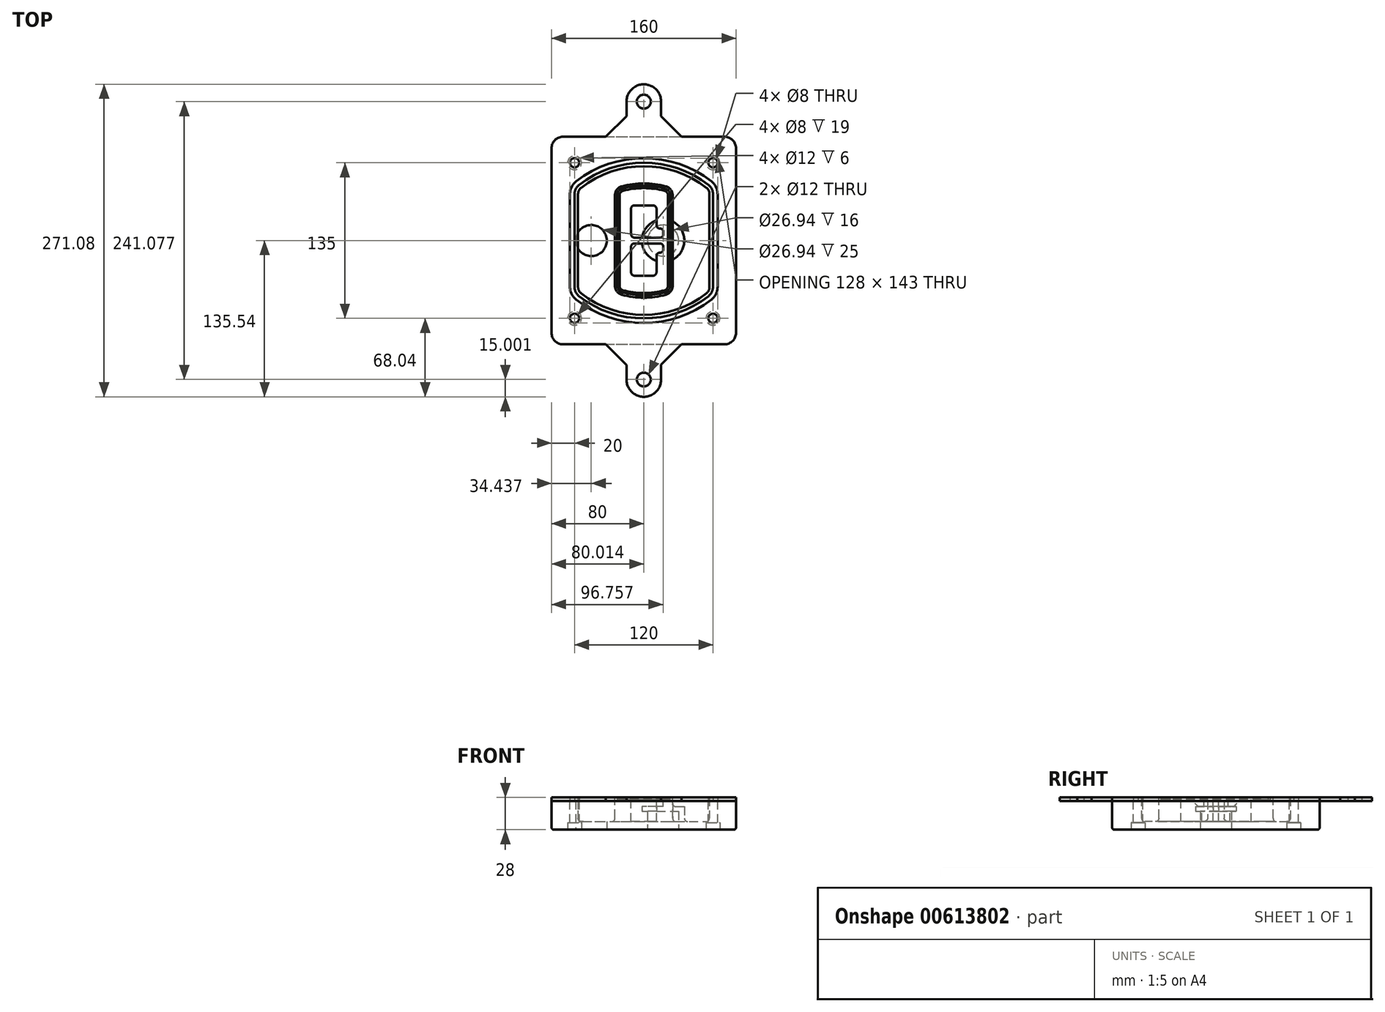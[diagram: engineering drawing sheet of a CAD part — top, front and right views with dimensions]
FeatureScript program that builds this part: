
annotation { "Feature Type Name" : "Feature", "Feature Type Description" : "" }
export const myFeature = defineFeature(function(context is Context, id is Id, definition is map)
    precondition{}
    {
        {
            var Q0;
            Q0=qCreatedBy(makeId("Top.planeOp"),FACE);
            var sketch = newSketch(context, id + "F0", { "sketchPlane" : qUnion([Q0])});
            skPoint(sketch, "E0.rect.middle", {"position": v(0, 0) * mm});
            skLineSegment(sketch, "E1.bottom", {"start": v(-70, -90) * mm, "end": v(70, -90) * mm});
            skLineSegment(sketch, "E1.top", {"start": v(-70, 90) * mm, "end": v(70, 90) * mm});
            skLineSegment(sketch, "E1.left", {"start": v(-80, -80) * mm, "end": v(-80, 80) * mm});
            skLineSegment(sketch, "E1.right", {"start": v(80, -80) * mm, "end": v(80, 80) * mm});
            skLineSegment(sketch, "E2", {"start": v(-80, 90) * mm, "end": v(80, -90) * mm, "construction": true});
            skLineSegment(sketch, "E3", {"start": v(80, 90) * mm, "end": v(-80, -90) * mm, "construction": true});
            skCircle(sketch, "E4", {"center": v(-60, 67.5) * mm, "radius": 4 * mm});
            skCircle(sketch, "E5", {"center": v(60, 67.5) * mm, "radius": 4 * mm});
            skCircle(sketch, "E6", {"center": v(60, -67.5) * mm, "radius": 4 * mm});
            skCircle(sketch, "E7", {"center": v(-60, -67.5) * mm, "radius": 4 * mm});
            skLineSegment(sketch, "E8", {"start": v(-60, 67.5) * mm, "end": v(60, 67.5) * mm, "construction": true});
            skLineSegment(sketch, "E9", {"start": v(60, 67.5) * mm, "end": v(60, -67.5) * mm, "construction": true});
            skLineSegment(sketch, "E10", {"start": v(60, -67.5) * mm, "end": v(-60, -67.5) * mm, "construction": true});
            skLineSegment(sketch, "E11", {"start": v(-60, -67.5) * mm, "end": v(-60, 67.5) * mm, "construction": true});
            skLineSegment(sketch, "E12", {"start": v(-60, 40.3) * mm, "end": v(-60, -40.3) * mm});
            skLineSegment(sketch, "E13", {"start": v(60, 40.3) * mm, "end": v(60, -40.3) * mm});
            skArc(sketch, "E14", {"start": v(56.15, 48.18) * mm, "mid": v(0, 67.5) * mm, "end": v(-56.15, 48.18) * mm});
            skArc(sketch, "E15", {"start": v(-56.15, -48.18) * mm, "mid": v(0, -67.5) * mm, "end": v(56.15, -48.18) * mm});
            skLineSegment(sketch, "E16", {"start": v(-60, 0) * mm, "end": v(60, 0) * mm, "construction": true});
            skPoint(sketch, "E17.visualSharp", {"position": v(-60, -45) * mm});
            skArc(sketch, "E17.filletArc", {"start": v(-60, -40.3) * mm, "mid": v(-58.99, -44.68) * mm, "end": v(-56.15, -48.18) * mm});
            skPoint(sketch, "E18.visualSharp", {"position": v(-60, 45) * mm});
            skArc(sketch, "E18.filletArc", {"start": v(-56.15, 48.18) * mm, "mid": v(-58.99, 44.68) * mm, "end": v(-60, 40.3) * mm});
            skPoint(sketch, "E19.visualSharp", {"position": v(60, 45) * mm});
            skArc(sketch, "E19.filletArc", {"start": v(60, 40.3) * mm, "mid": v(58.99, 44.68) * mm, "end": v(56.15, 48.18) * mm});
            skPoint(sketch, "E20.visualSharp", {"position": v(60, -45) * mm});
            skArc(sketch, "E20.filletArc", {"start": v(56.15, -48.18) * mm, "mid": v(58.99, -44.68) * mm, "end": v(60, -40.3) * mm});
            skPoint(sketch, "E21.visualSharp", {"position": v(-80, 90) * mm});
            skArc(sketch, "E21.filletArc", {"start": v(-70, 90) * mm, "mid": v(-77.07, 87.07) * mm, "end": v(-80, 80) * mm});
            skPoint(sketch, "E22.visualSharp", {"position": v(80, 90) * mm});
            skArc(sketch, "E22.filletArc", {"start": v(80, 80) * mm, "mid": v(77.07, 87.07) * mm, "end": v(70, 90) * mm});
            skPoint(sketch, "E23.visualSharp", {"position": v(80, -90) * mm});
            skArc(sketch, "E23.filletArc", {"start": v(70, -90) * mm, "mid": v(77.07, -87.07) * mm, "end": v(80, -80) * mm});
            skPoint(sketch, "E24.visualSharp", {"position": v(-80, -90) * mm});
            skArc(sketch, "E24.filletArc", {"start": v(-80, -80) * mm, "mid": v(-77.07, -87.07) * mm, "end": v(-70, -90) * mm});
            skArc(sketch, "E25.0", {"start": v(57, 40.3) * mm, "mid": v(56.3, 43.36) * mm, "end": v(54.3, 45.81) * mm});
            skLineSegment(sketch, "E25.1", {"start": v(57, 40.3) * mm, "end": v(57, -40.3) * mm});
            skArc(sketch, "E25.2", {"start": v(54.3, -45.81) * mm, "mid": v(56.3, -43.36) * mm, "end": v(57, -40.3) * mm});
            skArc(sketch, "E25.3", {"start": v(-54.3, -45.81) * mm, "mid": v(0, -64.5) * mm, "end": v(54.3, -45.81) * mm});
            skArc(sketch, "E25.4", {"start": v(-57, -40.3) * mm, "mid": v(-56.3, -43.36) * mm, "end": v(-54.3, -45.81) * mm});
            skArc(sketch, "E25.5", {"start": v(54.3, 45.81) * mm, "mid": v(0, 64.5) * mm, "end": v(-54.3, 45.81) * mm});
            skLineSegment(sketch, "E25.6", {"start": v(-57, 40.3) * mm, "end": v(-57, -40.3) * mm});
            skArc(sketch, "E25.7", {"start": v(-54.3, 45.81) * mm, "mid": v(-56.3, 43.36) * mm, "end": v(-57, 40.3) * mm});
            skArc(sketch, "E26.0", {"start": v(-58.62, 51.33) * mm, "mid": v(-62.58, 46.43) * mm, "end": v(-64, 40.3) * mm});
            skArc(sketch, "E26.1", {"start": v(58.62, 51.33) * mm, "mid": v(0, 71.5) * mm, "end": v(-58.62, 51.33) * mm});
            skArc(sketch, "E26.2", {"start": v(64, 40.3) * mm, "mid": v(62.58, 46.43) * mm, "end": v(58.62, 51.33) * mm});
            skLineSegment(sketch, "E26.3", {"start": v(64, 40.3) * mm, "end": v(64, -40.3) * mm});
            skArc(sketch, "E26.4", {"start": v(58.62, -51.33) * mm, "mid": v(62.58, -46.43) * mm, "end": v(64, -40.3) * mm});
            skLineSegment(sketch, "E26.5", {"start": v(-64, 40.3) * mm, "end": v(-64, -40.3) * mm});
            skArc(sketch, "E26.6", {"start": v(-58.62, -51.33) * mm, "mid": v(0, -71.5) * mm, "end": v(58.62, -51.33) * mm});
            skArc(sketch, "E26.7", {"start": v(-64, -40.3) * mm, "mid": v(-62.58, -46.43) * mm, "end": v(-58.62, -51.33) * mm});
            skArc(sketch, "E27", {"start": v(15.01, 120.3) * mm, "mid": v(0.13, 135.54) * mm, "end": v(-14.99, 120.54) * mm});
            skCircle(sketch, "E28", {"center": v(0.01, 120.54) * mm, "radius": 6 * mm});
            skLineSegment(sketch, "E29", {"start": v(0.01, 120.54) * mm, "end": v(0.01, 95) * mm, "construction": true});
            skLineSegment(sketch, "E30", {"start": v(-14.99, 120.54) * mm, "end": v(-14.99, 108) * mm});
            skLineSegment(sketch, "E31", {"start": v(-14.99, 108) * mm, "end": v(-32.99, 90) * mm});
            skLineSegment(sketch, "E32", {"start": v(15.01, 120.3) * mm, "end": v(15.01, 107.76) * mm});
            skPoint(sketch, "E32.endSnap0", {"position": v(0.01, 107.76) * mm});
            skLineSegment(sketch, "E33", {"start": v(15.01, 107.76) * mm, "end": v(32.78, 90) * mm});
            skLineSegment(sketch, "E34", {"start": v(-32.99, 90) * mm, "end": v(32.78, 90) * mm});
            skLineSegment(sketch, "E35", {"start": v(74.6, 0) * mm, "end": v(-74.47, 0) * mm, "construction": true});
            skLineSegment(sketch, "E36.MirrorCS", {"start": v(-14.99, -108) * mm, "end": v(-32.99, -90) * mm});
            skLineSegment(sketch, "E37.MirrorCS", {"start": v(-32.99, -90) * mm, "end": v(32.78, -90) * mm});
            skLineSegment(sketch, "E38.MirrorCS", {"start": v(15.01, -107.76) * mm, "end": v(32.78, -90) * mm});
            skCircle(sketch, "E39.MirrorC", {"center": v(0.01, -120.54) * mm, "radius": 6 * mm});
            skLineSegment(sketch, "E40.MirrorCS", {"start": v(0.01, -120.54) * mm, "end": v(0.01, -95) * mm, "construction": true});
            skLineSegment(sketch, "E41.MirrorCS", {"start": v(15.01, -120.3) * mm, "end": v(15.01, -107.76) * mm});
            skLineSegment(sketch, "E42.MirrorCS", {"start": v(-14.99, -120.54) * mm, "end": v(-14.99, -108) * mm});
            skArc(sketch, "E43.MirrorCS", {"start": v(15.01, -120.3) * mm, "mid": v(0.13, -135.54) * mm, "end": v(-14.99, -120.54) * mm});
            skPoint(sketch, "E44.MirrorP", {"position": v(0.01, -107.76) * mm});
            skSolve(sketch);
        }
        {
            var Q0;
            Q0=makeQuery(id+"F0.imprint","IMPRINT",FACE,{"disambiguationData":[TD([[makeQuery(id+"F0.imprint","IMPRINT",EDGE,{"derivedFrom":sQuery(id+"F0.wireOp",EDGE,"E1.bottom")}),1.0]])]});
            var Q1;
            Q1=makeQuery(id+"F0.imprint","IMPRINT",FACE,{"disambiguationData":[TD([[makeQuery(id+"F0.imprint","IMPRINT",EDGE,{"derivedFrom":sQuery(id+"F0.wireOp",EDGE,"E12")}),1.0]])]});
            var Q2;
            Q2=makeQuery(id+"F0.imprint","IMPRINT",FACE,{"disambiguationData":[TD([[makeQuery(id+"F0.imprint","IMPRINT",EDGE,{"derivedFrom":sQuery(id+"F0.wireOp",EDGE,"E25.0")}),1.0]])]});
            var Q3;
            Q3=makeQuery(id+"F0.imprint","IMPRINT",FACE,{"disambiguationData":[TD([[makeQuery(id+"F0.imprint","IMPRINT",EDGE,{"derivedFrom":sQuery(id+"F0.wireOp",EDGE,"E12")}),-1.0]])]});
            extrude(context, id + "F1", {"entities" : qUnion([Q0, Q1, Q2, Q3]), "oppositeDirection" : true, "depth" : 25 * mm});
        }
        {
            var Q0;
            Q0=makeQuery(id+"F0.imprint","IMPRINT",FACE,{"disambiguationData":[TD([[makeQuery(id+"F0.imprint","IMPRINT",EDGE,{"derivedFrom":sQuery(id+"F0.wireOp",EDGE,"E12")}),1.0]])]});
            extrude(context, id + "F2", {"entities" : qUnion([Q0]), "operationType" : NewBodyOperationType.ADD, "depth" : 3 * mm});
        }
        {
            var Q0;
            Q0=makeQuery(id+"F0.imprint","IMPRINT",FACE,{"disambiguationData":[TD([[makeQuery(id+"F0.imprint","IMPRINT",EDGE,{"derivedFrom":sQuery(id+"F0.wireOp",EDGE,"E25.0")}),1.0]])]});
            extrude(context, id + "F3", {"entities" : qUnion([Q0]), "operationType" : NewBodyOperationType.REMOVE, "oppositeDirection" : true, "depth" : 18 * mm});
        }
        {
            var Q0;
            Q0=makeQuery(id+"F2.opExtrude","CAP_FACE",FACE,{"disambiguationData":[OSD([sQuery(id+"F0.wireOp",EDGE,"E12"),sQuery(id+"F0.wireOp",EDGE,"E13"),sQuery(id+"F0.wireOp",EDGE,"E14"),sQuery(id+"F0.wireOp",EDGE,"E15"),sQuery(id+"F0.wireOp",EDGE,"E17.filletArc"),sQuery(id+"F0.wireOp",EDGE,"E18.filletArc"),sQuery(id+"F0.wireOp",EDGE,"E19.filletArc"),sQuery(id+"F0.wireOp",EDGE,"E20.filletArc"),sQuery(id+"F0.wireOp",EDGE,"E25.0"),sQuery(id+"F0.wireOp",EDGE,"E25.1"),sQuery(id+"F0.wireOp",EDGE,"E25.2"),sQuery(id+"F0.wireOp",EDGE,"E25.3"),sQuery(id+"F0.wireOp",EDGE,"E25.4"),sQuery(id+"F0.wireOp",EDGE,"E25.5"),sQuery(id+"F0.wireOp",EDGE,"E25.6"),sQuery(id+"F0.wireOp",EDGE,"E25.7")])],"isStart":false});
            var sketch = newSketch(context, id + "F4", { "sketchPlane" : qUnion([Q0])});
            skArc(sketch, "E45.0", {"start": v(-19.08, -46.97) * mm, "mid": v(0, -49.5) * mm, "end": v(19.08, -46.97) * mm});
            skArc(sketch, "E46.0", {"start": v(19.08, 46.97) * mm, "mid": v(0, 49.5) * mm, "end": v(-19.08, 46.97) * mm});
            skLineSegment(sketch, "E47", {"start": v(-25, 39.25) * mm, "end": v(-25, -39.25) * mm});
            skLineSegment(sketch, "E48", {"start": v(25, 39.25) * mm, "end": v(25, -39.25) * mm});
            skLineSegment(sketch, "E49", {"start": v(-25, 45.1) * mm, "end": v(25, 45.1) * mm, "construction": true});
            skLineSegment(sketch, "E50", {"start": v(-25, -45.1) * mm, "end": v(25, -45.1) * mm, "construction": true});
            skPoint(sketch, "E51.visualSharp", {"position": v(-25, 45.1) * mm});
            skArc(sketch, "E51.filletArc", {"start": v(-19.08, 46.97) * mm, "mid": v(-23.35, 44.11) * mm, "end": v(-25, 39.25) * mm});
            skPoint(sketch, "E52.visualSharp", {"position": v(25, 45.1) * mm});
            skArc(sketch, "E52.filletArc", {"start": v(25, 39.25) * mm, "mid": v(23.35, 44.11) * mm, "end": v(19.08, 46.97) * mm});
            skPoint(sketch, "E53.visualSharp", {"position": v(25, -45.1) * mm});
            skArc(sketch, "E53.filletArc", {"start": v(19.08, -46.97) * mm, "mid": v(23.35, -44.11) * mm, "end": v(25, -39.25) * mm});
            skPoint(sketch, "E54.visualSharp", {"position": v(-25, -45.1) * mm});
            skArc(sketch, "E54.filletArc", {"start": v(-25, -39.25) * mm, "mid": v(-23.35, -44.11) * mm, "end": v(-19.08, -46.97) * mm});
            skArc(sketch, "E55.0", {"start": v(54.3, 45.81) * mm, "mid": v(0, 64.5) * mm, "end": v(-54.3, 45.81) * mm});
            skArc(sketch, "E55.1", {"start": v(-54.3, 45.81) * mm, "mid": v(-56.3, 43.36) * mm, "end": v(-57, 40.3) * mm});
            skLineSegment(sketch, "E55.2", {"start": v(-57, 40.3) * mm, "end": v(-57, -40.3) * mm});
            skArc(sketch, "E55.3", {"start": v(-57, -40.3) * mm, "mid": v(-56.3, -43.36) * mm, "end": v(-54.3, -45.81) * mm});
            skArc(sketch, "E55.4", {"start": v(-54.3, -45.81) * mm, "mid": v(0, -64.5) * mm, "end": v(54.3, -45.81) * mm});
            skArc(sketch, "E55.5", {"start": v(54.3, -45.81) * mm, "mid": v(56.3, -43.36) * mm, "end": v(57, -40.3) * mm});
            skLineSegment(sketch, "E55.6", {"start": v(57, 40.3) * mm, "end": v(57, -40.3) * mm});
            skArc(sketch, "E55.7", {"start": v(57, 40.3) * mm, "mid": v(56.3, 43.36) * mm, "end": v(54.3, 45.81) * mm});
            skLineSegment(sketch, "E56.0", {"start": v(23, 39.25) * mm, "end": v(23, -39.25) * mm});
            skArc(sketch, "E56.1", {"start": v(18.56, -45.04) * mm, "mid": v(21.76, -42.9) * mm, "end": v(23, -39.25) * mm});
            skArc(sketch, "E56.2", {"start": v(-18.56, -45.04) * mm, "mid": v(0, -47.5) * mm, "end": v(18.56, -45.04) * mm});
            skArc(sketch, "E56.3", {"start": v(-23, -39.25) * mm, "mid": v(-21.76, -42.9) * mm, "end": v(-18.56, -45.04) * mm});
            skLineSegment(sketch, "E56.4", {"start": v(-23, 39.25) * mm, "end": v(-23, -39.25) * mm});
            skArc(sketch, "E56.5", {"start": v(23, 39.25) * mm, "mid": v(21.76, 42.9) * mm, "end": v(18.56, 45.04) * mm});
            skArc(sketch, "E56.6", {"start": v(-18.56, 45.04) * mm, "mid": v(-21.76, 42.9) * mm, "end": v(-23, 39.25) * mm});
            skArc(sketch, "E56.7", {"start": v(18.56, 45.04) * mm, "mid": v(0, 47.5) * mm, "end": v(-18.56, 45.04) * mm});
            skArc(sketch, "E57.0", {"start": v(21, 39.25) * mm, "mid": v(20.18, 41.68) * mm, "end": v(18.04, 43.1) * mm});
            skLineSegment(sketch, "E57.1", {"start": v(21, 39.25) * mm, "end": v(21, -39.25) * mm});
            skArc(sketch, "E57.2", {"start": v(18.04, -43.1) * mm, "mid": v(20.18, -41.68) * mm, "end": v(21, -39.25) * mm});
            skArc(sketch, "E57.3", {"start": v(-18.04, -43.1) * mm, "mid": v(0, -45.5) * mm, "end": v(18.04, -43.1) * mm});
            skArc(sketch, "E57.4", {"start": v(-21, -39.25) * mm, "mid": v(-20.18, -41.68) * mm, "end": v(-18.04, -43.1) * mm});
            skArc(sketch, "E57.5", {"start": v(18.04, 43.1) * mm, "mid": v(0, 45.5) * mm, "end": v(-18.04, 43.1) * mm});
            skLineSegment(sketch, "E57.6", {"start": v(-21, 39.25) * mm, "end": v(-21, -39.25) * mm});
            skArc(sketch, "E57.7", {"start": v(-18.04, 43.1) * mm, "mid": v(-20.18, 41.68) * mm, "end": v(-21, 39.25) * mm});
            skLineSegment(sketch, "E58", {"start": v(-25, 0) * mm, "end": v(25, 0) * mm, "construction": true});
            skLineSegment(sketch, "E59", {"start": v(-11, 5.5) * mm, "end": v(-11, 27.5) * mm});
            skLineSegment(sketch, "E60", {"start": v(-8, 30.5) * mm, "end": v(8, 30.5) * mm});
            skLineSegment(sketch, "E61", {"start": v(11, 27.5) * mm, "end": v(11, 13.5) * mm});
            skLineSegment(sketch, "E62", {"start": v(14, 10.5) * mm, "end": v(14, 10.5) * mm});
            skLineSegment(sketch, "E63", {"start": v(17, 7.5) * mm, "end": v(17, 5.5) * mm});
            skLineSegment(sketch, "E64", {"start": v(14, 2.5) * mm, "end": v(-8, 2.5) * mm});
            skPoint(sketch, "E65.visualSharp", {"position": v(-11, 30.5) * mm});
            skArc(sketch, "E65.filletArc", {"start": v(-8, 30.5) * mm, "mid": v(-10.12, 29.62) * mm, "end": v(-11, 27.5) * mm});
            skPoint(sketch, "E66.visualSharp", {"position": v(11, 30.5) * mm});
            skArc(sketch, "E66.filletArc", {"start": v(11, 27.5) * mm, "mid": v(10.12, 29.62) * mm, "end": v(8, 30.5) * mm});
            skPoint(sketch, "E67.visualSharp", {"position": v(11, 10.5) * mm});
            skArc(sketch, "E67.filletArc", {"start": v(11, 13.5) * mm, "mid": v(11.88, 11.38) * mm, "end": v(14, 10.5) * mm});
            skPoint(sketch, "E68.visualSharp", {"position": v(17, 10.5) * mm});
            skArc(sketch, "E68.filletArc", {"start": v(17, 7.5) * mm, "mid": v(16.12, 9.62) * mm, "end": v(14, 10.5) * mm});
            skPoint(sketch, "E69.visualSharp", {"position": v(17, 2.5) * mm});
            skArc(sketch, "E69.filletArc", {"start": v(14, 2.5) * mm, "mid": v(16.12, 3.38) * mm, "end": v(17, 5.5) * mm});
            skPoint(sketch, "E70.visualSharp", {"position": v(-11, 2.5) * mm});
            skArc(sketch, "E70.filletArc", {"start": v(-11, 5.5) * mm, "mid": v(-10.12, 3.38) * mm, "end": v(-8, 2.5) * mm});
            skLineSegment(sketch, "E71.0.MirrorCS", {"start": v(14, -2.5) * mm, "end": v(-8, -2.5) * mm});
            skArc(sketch, "E72.0.MirrorCS", {"start": v(-11, -5.5) * mm, "mid": v(-10.12, -3.38) * mm, "end": v(-8, -2.5) * mm});
            skLineSegment(sketch, "E73.0.MirrorCS", {"start": v(-11, -5.5) * mm, "end": v(-11, -27.5) * mm});
            skArc(sketch, "E74.0.MirrorCS", {"start": v(-8, -30.5) * mm, "mid": v(-10.12, -29.62) * mm, "end": v(-11, -27.5) * mm});
            skLineSegment(sketch, "E75.0.MirrorCS", {"start": v(-8, -30.5) * mm, "end": v(8, -30.5) * mm});
            skArc(sketch, "E76.0.MirrorCS", {"start": v(11, -27.5) * mm, "mid": v(10.12, -29.62) * mm, "end": v(8, -30.5) * mm});
            skLineSegment(sketch, "E77.0.MirrorCS", {"start": v(11, -27.5) * mm, "end": v(11, -13.5) * mm});
            skArc(sketch, "E78.0.MirrorCS", {"start": v(11, -13.5) * mm, "mid": v(11.88, -11.38) * mm, "end": v(14, -10.5) * mm});
            skArc(sketch, "E79.0.MirrorCS", {"start": v(17, -7.5) * mm, "mid": v(16.12, -9.62) * mm, "end": v(14, -10.5) * mm});
            skLineSegment(sketch, "E80.0.MirrorCS", {"start": v(17, -7.5) * mm, "end": v(17, -5.5) * mm});
            skArc(sketch, "E81.0.MirrorCS", {"start": v(14, -2.5) * mm, "mid": v(16.12, -3.38) * mm, "end": v(17, -5.5) * mm});
            skSolve(sketch);
        }
        {
            var Q0;
            Q0=makeQuery(id+"F4.imprint","IMPRINT",FACE,{"disambiguationData":[TD([[makeQuery(id+"F4.imprint","IMPRINT",EDGE,{"derivedFrom":sQuery(id+"F4.wireOp",EDGE,"E45.0")}),1.0]])]});
            var Q1;
            Q1=makeQuery(id+"F4.imprint","IMPRINT",FACE,{"disambiguationData":[TD([[makeQuery(id+"F4.imprint","IMPRINT",EDGE,{"derivedFrom":sQuery(id+"F4.wireOp",EDGE,"E56.0")}),-1.0]])]});
            var Q2;
            Q2=makeQuery(id+"F4.imprint","IMPRINT",FACE,{"disambiguationData":[TD([[makeQuery(id+"F4.imprint","IMPRINT",EDGE,{"derivedFrom":sQuery(id+"F4.wireOp",EDGE,"E57.0")}),1.0]])]});
            extrude(context, id + "F5", {"entities" : qUnion([Q0, Q1, Q2]), "operationType" : NewBodyOperationType.ADD, "endBound" : BoundingType.UP_TO_NEXT, "oppositeDirection" : true, "depth" : 25 * mm});
        }
        {
            var Q0;
            Q0=makeQuery(id+"F4.imprint","IMPRINT",FACE,{"disambiguationData":[TD([[makeQuery(id+"F4.imprint","IMPRINT",EDGE,{"derivedFrom":sQuery(id+"F4.wireOp",EDGE,"E56.0")}),-1.0]])]});
            extrude(context, id + "F6", {"entities" : qUnion([Q0]), "operationType" : NewBodyOperationType.REMOVE, "oppositeDirection" : true, "depth" : 2 * mm});
        }
        {
            var Q0;
            Q0=makeQuery(id+"F1.opExtrude","CAP_FACE",FACE,{"disambiguationData":[OSD([sQuery(id+"F0.wireOp",EDGE,"E1.bottom"),sQuery(id+"F0.wireOp",EDGE,"E1.top"),sQuery(id+"F0.wireOp",EDGE,"E1.left"),sQuery(id+"F0.wireOp",EDGE,"E1.right"),sQuery(id+"F0.wireOp",EDGE,"E4"),sQuery(id+"F0.wireOp",EDGE,"E5"),sQuery(id+"F0.wireOp",EDGE,"E6"),sQuery(id+"F0.wireOp",EDGE,"E7"),sQuery(id+"F0.wireOp",EDGE,"E21.filletArc"),sQuery(id+"F0.wireOp",EDGE,"E22.filletArc"),sQuery(id+"F0.wireOp",EDGE,"E23.filletArc"),sQuery(id+"F0.wireOp",EDGE,"E24.filletArc")])],"isStart":false});
            var sketch = newSketch(context, id + "F7", { "sketchPlane" : qUnion([Q0])});
            skCircle(sketch, "E82", {"center": v(16.76, 0) * mm, "radius": 13.47 * mm});
            skCircle(sketch, "E83", {"center": v(-45.56, 0) * mm, "radius": 13.47 * mm});
            skLineSegment(sketch, "E84", {"start": v(80, 0) * mm, "end": v(-80, 0) * mm});
            skCircle(sketch, "E85", {"center": v(16.76, 0) * mm, "radius": 18.47 * mm});
            skCircle(sketch, "E86", {"center": v(60, -67.5) * mm, "radius": 6 * mm});
            skCircle(sketch, "E87", {"center": v(-60, -67.5) * mm, "radius": 6 * mm});
            skCircle(sketch, "E88", {"center": v(-60, 67.5) * mm, "radius": 6 * mm});
            skCircle(sketch, "E89", {"center": v(60, 67.5) * mm, "radius": 6 * mm});
            skSolve(sketch);
        }
        {
            var Q0;
            {var subQ1=sQuery(id+"F7.wireOp",EDGE,"E84");var subQ4=sQuery(id+"F7.wireOp",EDGE,"E82");var subQ6=makeQuery(id+"F7.imprint","INTERSECT",VERTEX,{"disambiguationData":[OD(0.0)],"derivedFrom":[subQ4,subQ1]});Q0=makeQuery(id+"F7.imprint","IMPRINT",FACE,{"disambiguationData":[TD([[makeQuery(id+"F7.imprint","IMPRINT",EDGE,{"disambiguationData":[TD([[subQ6,-1.0]])],"derivedFrom":subQ4}),-1.0]])]});}
            var Q1;
            {var subQ0=sQuery(id+"F7.wireOp",EDGE,"E84");var subQ1=sQuery(id+"F7.wireOp",EDGE,"E82");var subQ3=makeQuery(id+"F7.imprint","INTERSECT",VERTEX,{"disambiguationData":[OD(0.0)],"derivedFrom":[subQ1,subQ0]});Q1=makeQuery(id+"F7.imprint","IMPRINT",FACE,{"disambiguationData":[TD([[makeQuery(id+"F7.imprint","IMPRINT",EDGE,{"disambiguationData":[TD([[subQ3,-1.0]])],"derivedFrom":subQ1}),1.0]])]});}
            var Q2;
            {var subQ0=sQuery(id+"F7.wireOp",EDGE,"E84");var subQ1=sQuery(id+"F7.wireOp",EDGE,"E82");var subQ3=makeQuery(id+"F7.imprint","INTERSECT",VERTEX,{"disambiguationData":[OD(0.0)],"derivedFrom":[subQ1,subQ0]});Q2=makeQuery(id+"F7.imprint","IMPRINT",FACE,{"disambiguationData":[TD([[makeQuery(id+"F7.imprint","IMPRINT",EDGE,{"disambiguationData":[TD([[subQ3,1.0]])],"derivedFrom":subQ1}),1.0]])]});}
            var Q3;
            {var subQ1=sQuery(id+"F7.wireOp",EDGE,"E84");var subQ4=sQuery(id+"F7.wireOp",EDGE,"E82");var subQ6=makeQuery(id+"F7.imprint","INTERSECT",VERTEX,{"disambiguationData":[OD(0.0)],"derivedFrom":[subQ4,subQ1]});Q3=makeQuery(id+"F7.imprint","IMPRINT",FACE,{"disambiguationData":[TD([[makeQuery(id+"F7.imprint","IMPRINT",EDGE,{"disambiguationData":[TD([[subQ6,1.0]])],"derivedFrom":subQ4}),-1.0]])]});}
            extrude(context, id + "F8", {"entities" : qUnion([Q0, Q1, Q2, Q3]), "operationType" : NewBodyOperationType.ADD, "oppositeDirection" : true, "depth" : 20 * mm});
        }
        {
            var Q0;
            {var subQ0=sQuery(id+"F7.wireOp",EDGE,"E84");var subQ1=sQuery(id+"F7.wireOp",EDGE,"E82");var subQ3=makeQuery(id+"F7.imprint","INTERSECT",VERTEX,{"disambiguationData":[OD(0.0)],"derivedFrom":[subQ1,subQ0]});Q0=makeQuery(id+"F7.imprint","IMPRINT",FACE,{"disambiguationData":[TD([[makeQuery(id+"F7.imprint","IMPRINT",EDGE,{"disambiguationData":[TD([[subQ3,-1.0]])],"derivedFrom":subQ1}),1.0]])]});}
            var Q1;
            {var subQ0=sQuery(id+"F7.wireOp",EDGE,"E84");var subQ1=sQuery(id+"F7.wireOp",EDGE,"E82");var subQ3=makeQuery(id+"F7.imprint","INTERSECT",VERTEX,{"disambiguationData":[OD(0.0)],"derivedFrom":[subQ1,subQ0]});Q1=makeQuery(id+"F7.imprint","IMPRINT",FACE,{"disambiguationData":[TD([[makeQuery(id+"F7.imprint","IMPRINT",EDGE,{"disambiguationData":[TD([[subQ3,1.0]])],"derivedFrom":subQ1}),1.0]])]});}
            extrude(context, id + "F9", {"entities" : qUnion([Q0, Q1]), "operationType" : NewBodyOperationType.REMOVE, "oppositeDirection" : true, "depth" : 16 * mm});
        }
        {
            var Q0;
            {var subQ0=sQuery(id+"F7.wireOp",EDGE,"E84");var subQ1=sQuery(id+"F7.wireOp",EDGE,"E83");var subQ3=makeQuery(id+"F7.imprint","INTERSECT",VERTEX,{"disambiguationData":[OD(0.0)],"derivedFrom":[subQ1,subQ0]});Q0=makeQuery(id+"F7.imprint","IMPRINT",FACE,{"disambiguationData":[TD([[makeQuery(id+"F7.imprint","IMPRINT",EDGE,{"disambiguationData":[TD([[subQ3,-1.0]])],"derivedFrom":subQ1}),1.0]])]});}
            var Q1;
            {var subQ0=sQuery(id+"F7.wireOp",EDGE,"E84");var subQ1=sQuery(id+"F7.wireOp",EDGE,"E83");var subQ3=makeQuery(id+"F7.imprint","INTERSECT",VERTEX,{"disambiguationData":[OD(0.0)],"derivedFrom":[subQ1,subQ0]});Q1=makeQuery(id+"F7.imprint","IMPRINT",FACE,{"disambiguationData":[TD([[makeQuery(id+"F7.imprint","IMPRINT",EDGE,{"disambiguationData":[TD([[subQ3,1.0]])],"derivedFrom":subQ1}),1.0]])]});}
            extrude(context, id + "F10", {"entities" : qUnion([Q0, Q1]), "operationType" : NewBodyOperationType.REMOVE, "oppositeDirection" : true, "depth" : 25 * mm});
        }
        {
            var Q0;
            Q0=makeQuery(id+"F7.imprint","IMPRINT",FACE,{"disambiguationData":[TD([[makeQuery(id+"F7.imprint","IMPRINT",EDGE,{"derivedFrom":sQuery(id+"F7.wireOp",EDGE,"E86")}),1.0]])]});
            var Q1;
            Q1=makeQuery(id+"F7.imprint","IMPRINT",FACE,{"disambiguationData":[TD([[makeQuery(id+"F7.imprint","IMPRINT",EDGE,{"derivedFrom":makeQuery(id+"F1.opExtrude","CAP_EDGE",EDGE,{"disambiguationData":[OSD([sQuery(id+"F0.wireOp",EDGE,"E5")])],"isStart":false})}),-1.0]])]});
            var Q2;
            Q2=makeQuery(id+"F7.imprint","IMPRINT",FACE,{"disambiguationData":[TD([[makeQuery(id+"F7.imprint","IMPRINT",EDGE,{"derivedFrom":sQuery(id+"F7.wireOp",EDGE,"E87")}),1.0]])]});
            var Q3;
            Q3=makeQuery(id+"F7.imprint","IMPRINT",FACE,{"disambiguationData":[TD([[makeQuery(id+"F7.imprint","IMPRINT",EDGE,{"derivedFrom":makeQuery(id+"F1.opExtrude","CAP_EDGE",EDGE,{"disambiguationData":[OSD([sQuery(id+"F0.wireOp",EDGE,"E4")])],"isStart":false})}),-1.0]])]});
            var Q4;
            Q4=makeQuery(id+"F7.imprint","IMPRINT",FACE,{"disambiguationData":[TD([[makeQuery(id+"F7.imprint","IMPRINT",EDGE,{"derivedFrom":sQuery(id+"F7.wireOp",EDGE,"E88")}),1.0]])]});
            var Q5;
            Q5=makeQuery(id+"F7.imprint","IMPRINT",FACE,{"disambiguationData":[TD([[makeQuery(id+"F7.imprint","IMPRINT",EDGE,{"derivedFrom":makeQuery(id+"F1.opExtrude","CAP_EDGE",EDGE,{"disambiguationData":[OSD([sQuery(id+"F0.wireOp",EDGE,"E7")])],"isStart":false})}),-1.0]])]});
            var Q6;
            Q6=makeQuery(id+"F7.imprint","IMPRINT",FACE,{"disambiguationData":[TD([[makeQuery(id+"F7.imprint","IMPRINT",EDGE,{"derivedFrom":sQuery(id+"F7.wireOp",EDGE,"E89")}),1.0]])]});
            var Q7;
            Q7=makeQuery(id+"F7.imprint","IMPRINT",FACE,{"disambiguationData":[TD([[makeQuery(id+"F7.imprint","IMPRINT",EDGE,{"derivedFrom":makeQuery(id+"F1.opExtrude","CAP_EDGE",EDGE,{"disambiguationData":[OSD([sQuery(id+"F0.wireOp",EDGE,"E6")])],"isStart":false})}),-1.0]])]});
            extrude(context, id + "F11", {"entities" : qUnion([Q0, Q1, Q2, Q3, Q4, Q5, Q6, Q7]), "operationType" : NewBodyOperationType.REMOVE, "oppositeDirection" : true, "depth" : 6 * mm});
        }
        {
            var Q0;
            Q0=makeQuery(id+"F9.boolean.opBoolean","COPY",FACE,{"derivedFrom":makeQuery(id+"F9.opExtrude","CAP_FACE",FACE,{"disambiguationData":[OSD([sQuery(id+"F7.wireOp",EDGE,"E82")])],"isStart":false})});
            var sketch = newSketch(context, id + "F12", { "sketchPlane" : qUnion([Q0])});
            skArc(sketch, "E90.0", {"start": v(11, 17.55) * mm, "mid": v(2.57, 11.82) * mm, "end": v(-1.54, 2.5) * mm});
            skArc(sketch, "E90.1", {"start": v(-1.54, -2.5) * mm, "mid": v(2.57, -11.82) * mm, "end": v(11, -17.55) * mm});
            skLineSegment(sketch, "E91", {"start": v(-1.54, -2.5) * mm, "end": v(14, -2.5) * mm});
            skLineSegment(sketch, "E92.0", {"start": v(14, 2.5) * mm, "end": v(-1.54, 2.5) * mm});
            skArc(sketch, "E92.1", {"start": v(14, 2.5) * mm, "mid": v(16.12, 3.38) * mm, "end": v(17, 5.5) * mm});
            skLineSegment(sketch, "E92.2", {"start": v(17, 7.5) * mm, "end": v(17, 5.5) * mm});
            skArc(sketch, "E92.3", {"start": v(17, 7.5) * mm, "mid": v(16.12, 9.62) * mm, "end": v(14, 10.5) * mm});
            skArc(sketch, "E92.4", {"start": v(11, 13.5) * mm, "mid": v(11.88, 11.38) * mm, "end": v(14, 10.5) * mm});
            skLineSegment(sketch, "E92.5", {"start": v(11, 17.55) * mm, "end": v(11, 13.5) * mm});
            skLineSegment(sketch, "E92.7", {"start": v(14, -2.5) * mm, "end": v(-1.54, -2.5) * mm});
            skArc(sketch, "E92.8", {"start": v(14, -2.5) * mm, "mid": v(16.12, -3.38) * mm, "end": v(17, -5.5) * mm});
            skLineSegment(sketch, "E92.9", {"start": v(17, -7.5) * mm, "end": v(17, -5.5) * mm});
            skArc(sketch, "E92.10", {"start": v(17, -7.5) * mm, "mid": v(16.12, -9.62) * mm, "end": v(14, -10.5) * mm});
            skArc(sketch, "E92.11", {"start": v(11, -13.5) * mm, "mid": v(11.88, -11.38) * mm, "end": v(14, -10.5) * mm});
            skLineSegment(sketch, "E92.12", {"start": v(11, -17.55) * mm, "end": v(11, -13.5) * mm});
            skPoint(sketch, "E93.orphan", {"position": v(11, -27.5) * mm});
            skPoint(sketch, "E94.orphan", {"position": v(-8, -2.5) * mm});
            skPoint(sketch, "E95.orphan", {"position": v(-8, 2.5) * mm});
            skPoint(sketch, "E96.orphan", {"position": v(11, 27.5) * mm});
            skSolve(sketch);
        }
        {
            var Q0;
            {var subQ7=sQuery(id+"F12.wireOp",EDGE,"E90.0");var subQ14=sQuery(id+"F12.wireOp",EDGE,"E90.1");var subQ16=sQuery(id+"F12.wireOp",EDGE,"E92.1");var subQ18=sQuery(id+"F12.wireOp",EDGE,"E92.8");Q0=qUnion([makeQuery(id+"F12.imprint","IMPRINT",FACE,{"disambiguationData":[TD([[makeQuery(id+"F12.imprint","IMPRINT",EDGE,{"derivedFrom":subQ7}),1.0]])]}),makeQuery(id+"F12.imprint","IMPRINT",FACE,{"disambiguationData":[TD([[makeQuery(id+"F12.imprint","IMPRINT",EDGE,{"derivedFrom":subQ14}),1.0]])]}),makeQuery(id+"F12.imprint","IMPRINT",FACE,{"disambiguationData":[TD([[makeQuery(id+"F12.imprint","IMPRINT",EDGE,{"derivedFrom":subQ16}),1.0]])]}),makeQuery(id+"F12.imprint","IMPRINT",FACE,{"disambiguationData":[TD([[makeQuery(id+"F12.imprint","IMPRINT",EDGE,{"derivedFrom":subQ18}),-1.0]])]})]);}
            var Q1;
            Q1=makeQuery(id+"F5.boolean.opBoolean","SPLIT",FACE,{"disambiguationData":[TD([makeQuery(id+"F5.opExtrude","SWEPT_FACE",FACE,{"disambiguationData":[OSD([sQuery(id+"F4.wireOp",EDGE,"E59")])]})])],"derivedFrom":makeQuery(id+"F3.boolean.opBoolean","COPY",FACE,{"derivedFrom":makeQuery(id+"F3.opExtrude","CAP_FACE",FACE,{"disambiguationData":[OSD([sQuery(id+"F0.wireOp",EDGE,"E25.0"),sQuery(id+"F0.wireOp",EDGE,"E25.1"),sQuery(id+"F0.wireOp",EDGE,"E25.2"),sQuery(id+"F0.wireOp",EDGE,"E25.3"),sQuery(id+"F0.wireOp",EDGE,"E25.4"),sQuery(id+"F0.wireOp",EDGE,"E25.5"),sQuery(id+"F0.wireOp",EDGE,"E25.6"),sQuery(id+"F0.wireOp",EDGE,"E25.7")])],"isStart":false})})});
            extrude(context, id + "F13", {"entities" : qUnion([Q0]), "operationType" : NewBodyOperationType.REMOVE, "endBound" : BoundingType.UP_TO_SURFACE, "endBoundEntityFace" : qUnion([Q1]), "depth" : 25 * mm});
        }
        {
            var Q0;
            Q0=makeQuery(id+"F3.boolean.opBoolean","COPY",EDGE,{"derivedFrom":makeQuery(id+"F3.opExtrude","CAP_EDGE",EDGE,{"disambiguationData":[OSD([sQuery(id+"F0.wireOp",EDGE,"E25.6")])],"isStart":false})});
            var Q1;
            Q1=makeQuery(id+"F8.boolean.opBoolean","INTERSECT",EDGE,{"derivedFrom":[makeQuery(id+"F5.opExtrude","SWEPT_FACE",FACE,{"disambiguationData":[OSD([sQuery(id+"F4.wireOp",EDGE,"E48")])]}),makeQuery(id+"F8.opExtrude","CAP_FACE",FACE,{"disambiguationData":[OSD([sQuery(id+"F7.wireOp",EDGE,"E85")])],"isStart":false})]});
            var Q2;
            Q2=makeQuery(id+"F8.boolean.opBoolean","INTERSECT",EDGE,{"disambiguationData":[OD(1.0)],"derivedFrom":[makeQuery(id+"F5.opExtrude","SWEPT_FACE",FACE,{"disambiguationData":[OSD([sQuery(id+"F4.wireOp",EDGE,"E48")])]}),makeQuery(id+"F8.opExtrude","SWEPT_FACE",FACE,{"disambiguationData":[OSD([sQuery(id+"F7.wireOp",EDGE,"E85")])]})]});
            var Q3;
            {var subQ0=sQuery(id+"F4.wireOp",EDGE,"E48");Q3=makeQuery(id+"F8.boolean.opBoolean","SPLIT",EDGE,{"disambiguationData":[TD([makeQuery(id+"F5.opExtrude","SWEPT_FACE",FACE,{"disambiguationData":[OSD([sQuery(id+"F4.wireOp",EDGE,"E53.filletArc")])]})])],"derivedFrom":makeQuery(id+"F5.opExtrude","CAP_EDGE",EDGE,{"disambiguationData":[OSD([subQ0])],"isStart":false})});}
            var Q4;
            {var subQ0=sQuery(id+"F0.wireOp",EDGE,"E25.7");var subQ1=sQuery(id+"F0.wireOp",EDGE,"E25.1");var subQ2=sQuery(id+"F0.wireOp",EDGE,"E25.6");var subQ3=sQuery(id+"F0.wireOp",EDGE,"E25.5");var subQ4=sQuery(id+"F0.wireOp",EDGE,"E25.4");var subQ5=sQuery(id+"F0.wireOp",EDGE,"E25.0");var subQ6=sQuery(id+"F0.wireOp",EDGE,"E25.2");var subQ7=sQuery(id+"F0.wireOp",EDGE,"E25.3");Q4=makeQuery(id+"F8.boolean.opBoolean","INTERSECT",EDGE,{"derivedFrom":[makeQuery(id+"F5.boolean.opBoolean","SPLIT",FACE,{"disambiguationData":[TD([makeQuery(id+"F2.opExtrude","SWEPT_FACE",FACE,{"disambiguationData":[OSD([subQ5])]})])],"derivedFrom":makeQuery(id+"F3.boolean.opBoolean","COPY",FACE,{"derivedFrom":makeQuery(id+"F3.opExtrude","CAP_FACE",FACE,{"disambiguationData":[OSD([subQ5,subQ1,subQ6,subQ7,subQ4,subQ3,subQ2,subQ0])],"isStart":false})})}),makeQuery(id+"F8.opExtrude","SWEPT_FACE",FACE,{"disambiguationData":[OSD([sQuery(id+"F7.wireOp",EDGE,"E85")])]})]});}
            var Q5;
            Q5=makeQuery(id+"F8.boolean.opBoolean","INTERSECT",EDGE,{"disambiguationData":[OD(0.0)],"derivedFrom":[makeQuery(id+"F5.opExtrude","SWEPT_FACE",FACE,{"disambiguationData":[OSD([sQuery(id+"F4.wireOp",EDGE,"E48")])]}),makeQuery(id+"F8.opExtrude","SWEPT_FACE",FACE,{"disambiguationData":[OSD([sQuery(id+"F7.wireOp",EDGE,"E85")])]})]});
            fillet(context, id + "F14", {"entities" : qUnion([Q0, Q1, Q2, Q3, Q4, Q5]), "radius" : 3 * mm, "tangentPropagation" : true, "allowEdgeOverflow" : false});
        }
        {
            var Q0;
            Q0=makeQuery(id+"F1.opExtrude","CAP_EDGE",EDGE,{"disambiguationData":[OSD([sQuery(id+"F0.wireOp",EDGE,"E1.bottom")])],"isStart":false});
            fillet(context, id + "F15", {"entities" : qUnion([Q0]), "radius" : 2 * mm, "tangentPropagation" : true, "allowEdgeOverflow" : false});
        }
        {
            var Q0;
            Q0 = qSketchRegion(id + "F0", true);
            var Q1;
            Q1=makeQuery(id+"F2.opExtrude","CAP_FACE",FACE,{"disambiguationData":[OSD([sQuery(id+"F0.wireOp",EDGE,"E12"),sQuery(id+"F0.wireOp",EDGE,"E13"),sQuery(id+"F0.wireOp",EDGE,"E14"),sQuery(id+"F0.wireOp",EDGE,"E15"),sQuery(id+"F0.wireOp",EDGE,"E17.filletArc"),sQuery(id+"F0.wireOp",EDGE,"E18.filletArc"),sQuery(id+"F0.wireOp",EDGE,"E19.filletArc"),sQuery(id+"F0.wireOp",EDGE,"E20.filletArc"),sQuery(id+"F0.wireOp",EDGE,"E25.0"),sQuery(id+"F0.wireOp",EDGE,"E25.1"),sQuery(id+"F0.wireOp",EDGE,"E25.2"),sQuery(id+"F0.wireOp",EDGE,"E25.3"),sQuery(id+"F0.wireOp",EDGE,"E25.4"),sQuery(id+"F0.wireOp",EDGE,"E25.5"),sQuery(id+"F0.wireOp",EDGE,"E25.6"),sQuery(id+"F0.wireOp",EDGE,"E25.7")])],"isStart":false});
            extrude(context, id + "F16", {"entities" : qUnion([Q0]), "endBound" : BoundingType.UP_TO_SURFACE, "depth" : 25 * mm, "endBoundEntityFace" : qUnion([Q1]), "offsetDistance" : 25 * mm});
        }
    });
